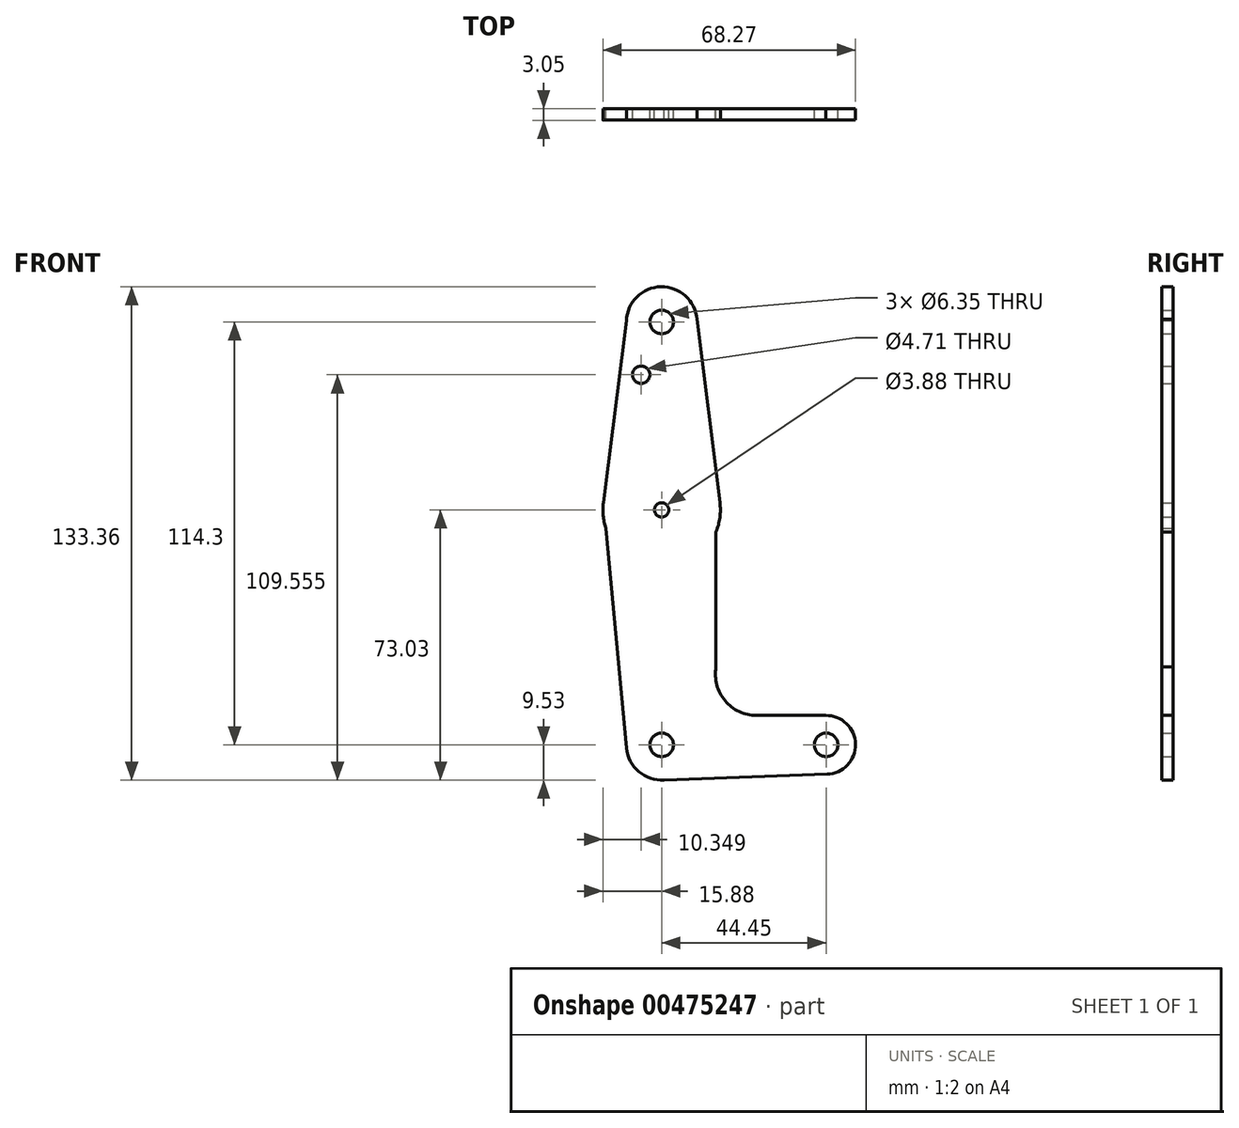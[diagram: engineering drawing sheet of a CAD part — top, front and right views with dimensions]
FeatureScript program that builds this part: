
annotation { "Feature Type Name" : "Feature", "Feature Type Description" : "" }
export const myFeature = defineFeature(function(context is Context, id is Id, definition is map)
    precondition{}
    {
        {
            var Q0;
            Q0=qCreatedBy(makeId("Front.planeOp"),FACE);
            var sketch = newSketch(context, id + "F0", { "sketchPlane" : qUnion([Q0])});
            skCircle(sketch, "E0", {"center": v(0, 0) * mm, "radius": 9.53 * mm});
            skCircle(sketch, "E1", {"center": v(0, 63.5) * mm, "radius": 15.88 * mm});
            skCircle(sketch, "E2", {"center": v(0, 114.3) * mm, "radius": 9.53 * mm});
            skCircle(sketch, "E3", {"center": v(44.45, 0) * mm, "radius": 7.94 * mm});
            skLineSegment(sketch, "E4", {"start": v(0, 114.3) * mm, "end": v(0, 0) * mm, "construction": true});
            skLineSegment(sketch, "E5", {"start": v(0, 0) * mm, "end": v(44.45, 0) * mm, "construction": true});
            skCircle(sketch, "E6", {"center": v(-5.53, 100.03) * mm, "radius": 2.36 * mm});
            skCircle(sketch, "E7", {"center": v(0, 114.3) * mm, "radius": 3.18 * mm});
            skCircle(sketch, "E8", {"center": v(0, 0) * mm, "radius": 3.18 * mm});
            skCircle(sketch, "E9", {"center": v(44.45, 0) * mm, "radius": 3.18 * mm});
            skLineSegment(sketch, "E10", {"start": v(-9.52, 114.61) * mm, "end": v(-15.75, 65.5) * mm});
            skLineSegment(sketch, "E11", {"start": v(9.5, 115.02) * mm, "end": v(15.75, 65.5) * mm});
            skLineSegment(sketch, "E12", {"start": v(-15.75, 65.5) * mm, "end": v(-9.48, -0.9) * mm});
            skLineSegment(sketch, "E13", {"start": v(14.7, 57.51) * mm, "end": v(14.7, 21.01) * mm});
            skLineSegment(sketch, "E14", {"start": v(44.57, 7.94) * mm, "end": v(25.67, 7.94) * mm});
            skArc(sketch, "E15", {"start": v(14.7, 21.01) * mm, "mid": v(17.14, 11.92) * mm, "end": v(25.67, 7.94) * mm});
            skLineSegment(sketch, "E16", {"start": v(0, -9.53) * mm, "end": v(44.73, -7.93) * mm});
            skCircle(sketch, "E17", {"center": v(0, 63.5) * mm, "radius": 1.94 * mm});
            skSolve(sketch);
        }
        {
            var Q0;
            Q0 = qSketchRegion(id + "F0", true);
            extrude(context, id + "F1", {"entities" : qUnion([Q0]), "depth" : 3.05 * mm});
        }
    });
